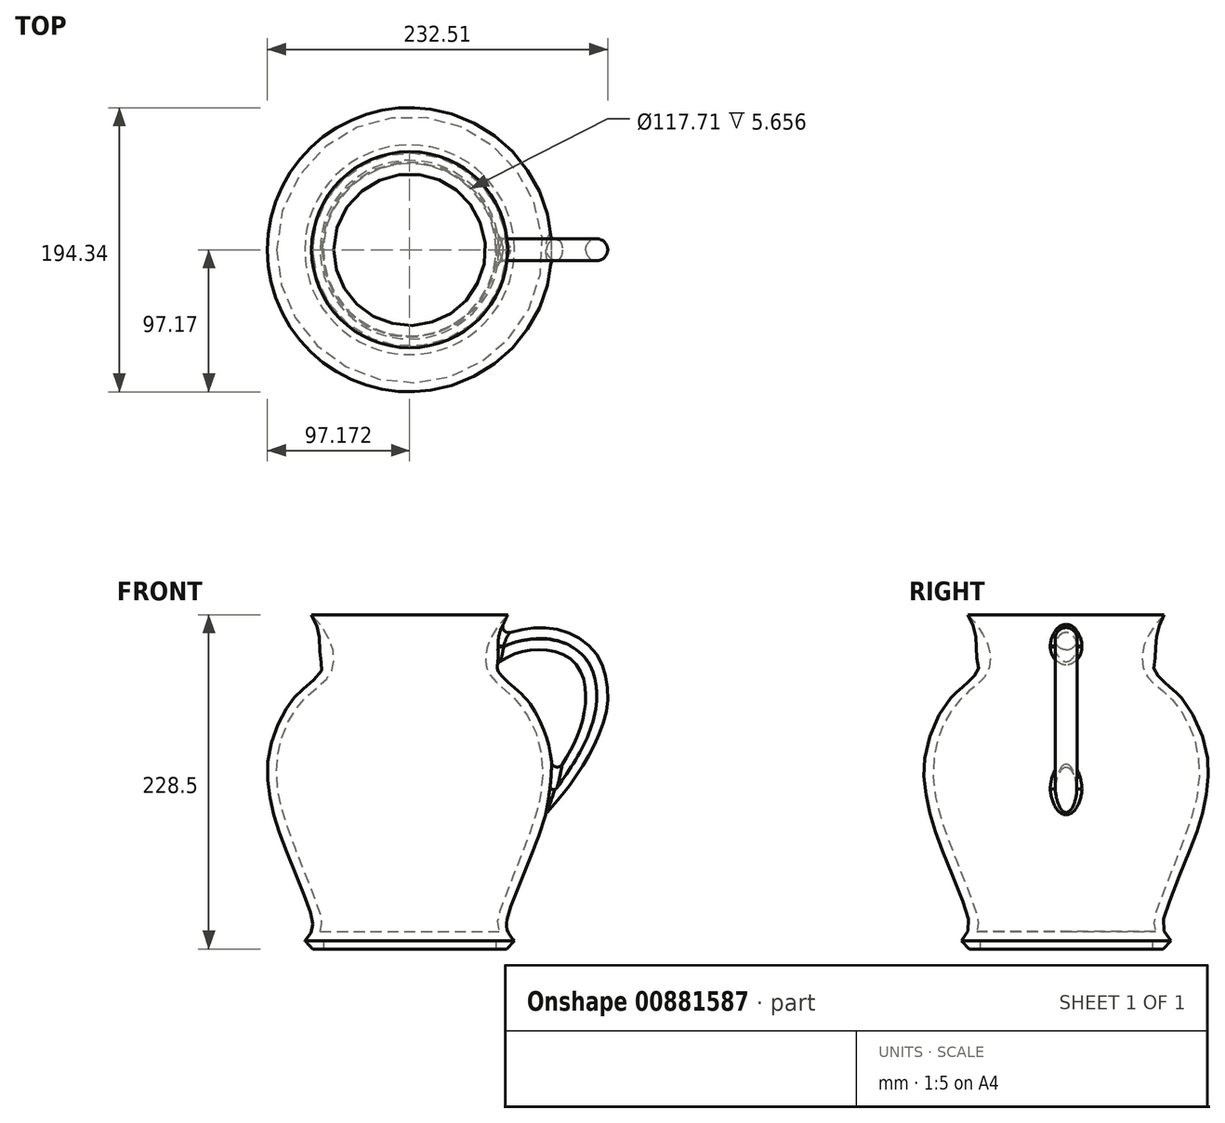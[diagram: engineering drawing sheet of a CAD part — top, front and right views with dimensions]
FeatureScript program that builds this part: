
annotation { "Feature Type Name" : "Feature", "Feature Type Description" : "" }
export const myFeature = defineFeature(function(context is Context, id is Id, definition is map)
    precondition{}
    {
        {
            var Q0;
            Q0=qCreatedBy(makeId("Front.planeOp"),FACE);
            var sketch = newSketch(context, id + "F0", { "sketchPlane" : qUnion([Q0])});
            skLineSegment(sketch, "E0", {"start": v(-91, -76.43) * mm, "end": v(-91, 128.57) * mm});
            skFitSpline(sketch, "E1", {"points": [v(106.32, 38.02) * mm, v(126.52, 74.76) * mm, v(128.18, 110.24) * mm, v(111.92, 126.25) * mm, v(88.27, 127.43) * mm, v(77.32, 123.55) * mm, v(68.3, 116.62) * mm], "startDerivative": vector(115.73, 175.54) * mm, "endDerivative": vector(-24.96, -74.89) * mm});
            skFitSpline(sketch, "E2", {"points": [v(103.08, 16.5) * mm, v(126.92, 47.05) * mm, v(142.83, 80.17) * mm, v(144.87, 103.29) * mm, v(135.93, 127.35) * mm, v(103.18, 143.42) * mm, v(73.57, 138.52) * mm, v(69.7, 138.2) * mm], "startDerivative": vector(159.27, 173.16) * mm, "endDerivative": vector(-120.13, 30.19) * mm});
            skLineSegment(sketch, "E3", {"start": v(69.7, 138.2) * mm, "end": v(68.3, 116.62) * mm});
            skLineSegment(sketch, "E4", {"start": v(106.32, 38.02) * mm, "end": v(103.08, 16.5) * mm});
            skSolve(sketch);
        }
        {
            var Q0;
            Q0=makeQuery(id+"F0.imprint","IMPRINT",FACE,{"disambiguationData":[TD([[makeQuery(id+"F0.imprint","IMPRINT",EDGE,{"derivedFrom":sQuery(id+"F0.wireOp",EDGE,"E1")}),-1.0]])]});
            extrude(context, id + "F1", {"entities" : qUnion([Q0]), "endBound" : BoundingType.SYMMETRIC, "depth" : 15 * mm, "offsetDistance" : 25 * mm});
        }
        {
            var Q0;
            Q0=makeQuery(id+"F1.opExtrude","CAP_EDGE",EDGE,{"disambiguationData":[OSD([sQuery(id+"F0.wireOp",EDGE,"E2")])],"isStart":false});
            var Q1;
            Q1=makeQuery(id+"F1.opExtrude","CAP_EDGE",EDGE,{"disambiguationData":[OSD([sQuery(id+"F0.wireOp",EDGE,"E2")])],"isStart":true});
            var Q2;
            Q2=makeQuery(id+"F1.opExtrude","CAP_EDGE",EDGE,{"disambiguationData":[OSD([sQuery(id+"F0.wireOp",EDGE,"E1")])],"isStart":true});
            var Q3;
            Q3=makeQuery(id+"F1.opExtrude","CAP_EDGE",EDGE,{"disambiguationData":[OSD([sQuery(id+"F0.wireOp",EDGE,"E1")])],"isStart":false});
            fillet(context, id + "F2", {"entities" : qUnion([Q0, Q1, Q2, Q3]), "radius" : 7.5 * mm, "tangentPropagation" : true, "allowEdgeOverflow" : false});
        }
        {
            var Q0;
            Q0=qCreatedBy(makeId("Front.planeOp"),FACE);
            var sketch = newSketch(context, id + "F3", { "sketchPlane" : qUnion([Q0])});
            skLineSegment(sketch, "E5", {"start": v(68.75, -70.61) * mm, "end": v(68.75, -76.27) * mm});
            skLineSegment(sketch, "E6", {"start": v(68.75, -76.27) * mm, "end": v(76.16, -76.27) * mm});
            skLineSegment(sketch, "E7", {"start": v(76.16, -76.27) * mm, "end": v(81.53, -70.61) * mm});
            skLineSegment(sketch, "E8", {"start": v(71.04, -64.26) * mm, "end": v(9.77, -64.26) * mm});
            skLineSegment(sketch, "E9", {"start": v(68.75, -70.61) * mm, "end": v(9.9, -70.61) * mm});
            skFitSpline(sketch, "E10", {"points": [v(81.53, -70.61) * mm, v(76.54, -62.93) * mm, v(77.7, -51.47) * mm, v(94.95, -7.5) * mm, v(105.19, 26.34) * mm, v(105.55, 60.27) * mm, v(92.43, 90.87) * mm, v(81.53, 102.3) * mm, v(69.95, 114.59) * mm, v(70.68, 121.37) * mm, v(71.73, 138.84) * mm, v(76.93, 152.23) * mm], "startDerivative": vector(-120.8, 119.44) * mm, "endDerivative": vector(107.22, 236.1) * mm});
            skFitSpline(sketch, "E11", {"points": [v(71.04, -64.26) * mm, v(69.9, -58.25) * mm, v(71.89, -49.41) * mm, v(88.79, -5.46) * mm, v(100.46, 36.24) * mm, v(96.02, 71.78) * mm, v(79.89, 96.73) * mm, v(65.9, 109.21) * mm, v(61.94, 119) * mm, v(63.52, 132.27) * mm, v(76.93, 152.23) * mm], "startDerivative": vector(-29.71, 112) * mm, "endDerivative": vector(153.63, 133.04) * mm});
            skLineSegment(sketch, "E12", {"start": v(9.9, -70.61) * mm, "end": v(9.9, 157.3) * mm});
            skSolve(sketch);
        }
        {
            var Q0;
            Q0 = qSketchRegion(id + "F3", true);
            var Q1;
            Q1=sQuery(id+"F3.wireOp",EDGE,"E12");
            revolve(context, id + "F4", {"operationType" : NewBodyOperationType.ADD, "surfaceOperationType" : NewSurfaceOperationType.NEW, "entities" : qUnion([Q0]), "axis" : qUnion([Q1]), "revolveType" : RevolveType.FULL});
        }
        {
            var Q0;
            {var subQ0=sQuery(id+"F0.wireOp",EDGE,"E1");Q0=makeQuery(id+"F4.boolean.opBoolean","INTERSECT",EDGE,{"disambiguationData":[OD(1.0)],"derivedFrom":[makeQuery(id+"F2.opFillet","BLEND_FACE",FACE,{"disambiguationData":[OSD([subQ0]),TDD([makeQuery(id+"F1.opExtrude","CAP_EDGE",EDGE,{"disambiguationData":[OSD([subQ0])],"isStart":false})])]}),makeQuery(id+"F4.opRevolve","SWEPT_FACE",FACE,{"disambiguationData":[OSD([sQuery(id+"F3.wireOp",EDGE,"E10")])]})]});}
            var Q1;
            {var subQ0=sQuery(id+"F0.wireOp",EDGE,"E2");Q1=makeQuery(id+"F4.boolean.opBoolean","INTERSECT",EDGE,{"disambiguationData":[OD(1.0)],"derivedFrom":[makeQuery(id+"F2.opFillet","BLEND_FACE",FACE,{"disambiguationData":[OSD([subQ0]),TDD([makeQuery(id+"F1.opExtrude","CAP_EDGE",EDGE,{"disambiguationData":[OSD([subQ0])],"isStart":true})])]}),makeQuery(id+"F4.opRevolve","SWEPT_FACE",FACE,{"disambiguationData":[OSD([sQuery(id+"F3.wireOp",EDGE,"E10")])]})]});}
            var Q2;
            {var subQ0=sQuery(id+"F0.wireOp",EDGE,"E1");Q2=makeQuery(id+"F4.boolean.opBoolean","INTERSECT",EDGE,{"disambiguationData":[OD(0.0)],"derivedFrom":[makeQuery(id+"F2.opFillet","BLEND_FACE",FACE,{"disambiguationData":[OSD([subQ0]),TDD([makeQuery(id+"F1.opExtrude","CAP_EDGE",EDGE,{"disambiguationData":[OSD([subQ0])],"isStart":true})])]}),makeQuery(id+"F4.opRevolve","SWEPT_FACE",FACE,{"disambiguationData":[OSD([sQuery(id+"F3.wireOp",EDGE,"E10")])]})]});}
            var Q3;
            Q3=makeQuery(id+"F2.opFillet","BLEND_EDGE",EDGE,{"blendedFrom":[makeQuery(id+"F1.opExtrude","CAP_EDGE",EDGE,{"disambiguationData":[OSD([sQuery(id+"F0.wireOp",EDGE,"E2")])],"isStart":true}),makeQuery(id+"F1.opExtrude","SWEPT_FACE",FACE,{"disambiguationData":[OSD([sQuery(id+"F0.wireOp",EDGE,"E4")])]})],"blendedInto":[makeQuery(id+"F1.opExtrude","SWEPT_FACE",FACE,{"disambiguationData":[OSD([sQuery(id+"F0.wireOp",EDGE,"E4")])]})]});
            var Q4;
            Q4=makeQuery(id+"F2.opFillet","BLEND_EDGE",EDGE,{"blendedFrom":[makeQuery(id+"F1.opExtrude","CAP_EDGE",EDGE,{"disambiguationData":[OSD([sQuery(id+"F0.wireOp",EDGE,"E2")])],"isStart":false}),makeQuery(id+"F1.opExtrude","SWEPT_FACE",FACE,{"disambiguationData":[OSD([sQuery(id+"F0.wireOp",EDGE,"E4")])]})],"blendedInto":[makeQuery(id+"F1.opExtrude","SWEPT_FACE",FACE,{"disambiguationData":[OSD([sQuery(id+"F0.wireOp",EDGE,"E4")])]})]});
            var Q5;
            {var subQ0=sQuery(id+"F0.wireOp",EDGE,"E2");Q5=makeQuery(id+"F4.boolean.opBoolean","INTERSECT",EDGE,{"disambiguationData":[OD(1.0)],"derivedFrom":[makeQuery(id+"F2.opFillet","BLEND_FACE",FACE,{"disambiguationData":[OSD([subQ0]),TDD([makeQuery(id+"F1.opExtrude","CAP_EDGE",EDGE,{"disambiguationData":[OSD([subQ0])],"isStart":false})])]}),makeQuery(id+"F4.opRevolve","SWEPT_FACE",FACE,{"disambiguationData":[OSD([sQuery(id+"F3.wireOp",EDGE,"E10")])]})]});}
            var Q6;
            {var subQ0=sQuery(id+"F0.wireOp",EDGE,"E1");Q6=makeQuery(id+"F4.boolean.opBoolean","INTERSECT",EDGE,{"disambiguationData":[OD(0.0)],"derivedFrom":[makeQuery(id+"F2.opFillet","BLEND_FACE",FACE,{"disambiguationData":[OSD([subQ0]),TDD([makeQuery(id+"F1.opExtrude","CAP_EDGE",EDGE,{"disambiguationData":[OSD([subQ0])],"isStart":false})])]}),makeQuery(id+"F4.opRevolve","SWEPT_FACE",FACE,{"disambiguationData":[OSD([sQuery(id+"F3.wireOp",EDGE,"E10")])]})]});}
            fillet(context, id + "F5", {"entities" : qUnion([Q0, Q1, Q2, Q3, Q4, Q5, Q6]), "radius" : 4 * mm, "tangentPropagation" : true, "allowEdgeOverflow" : false});
        }
    });
